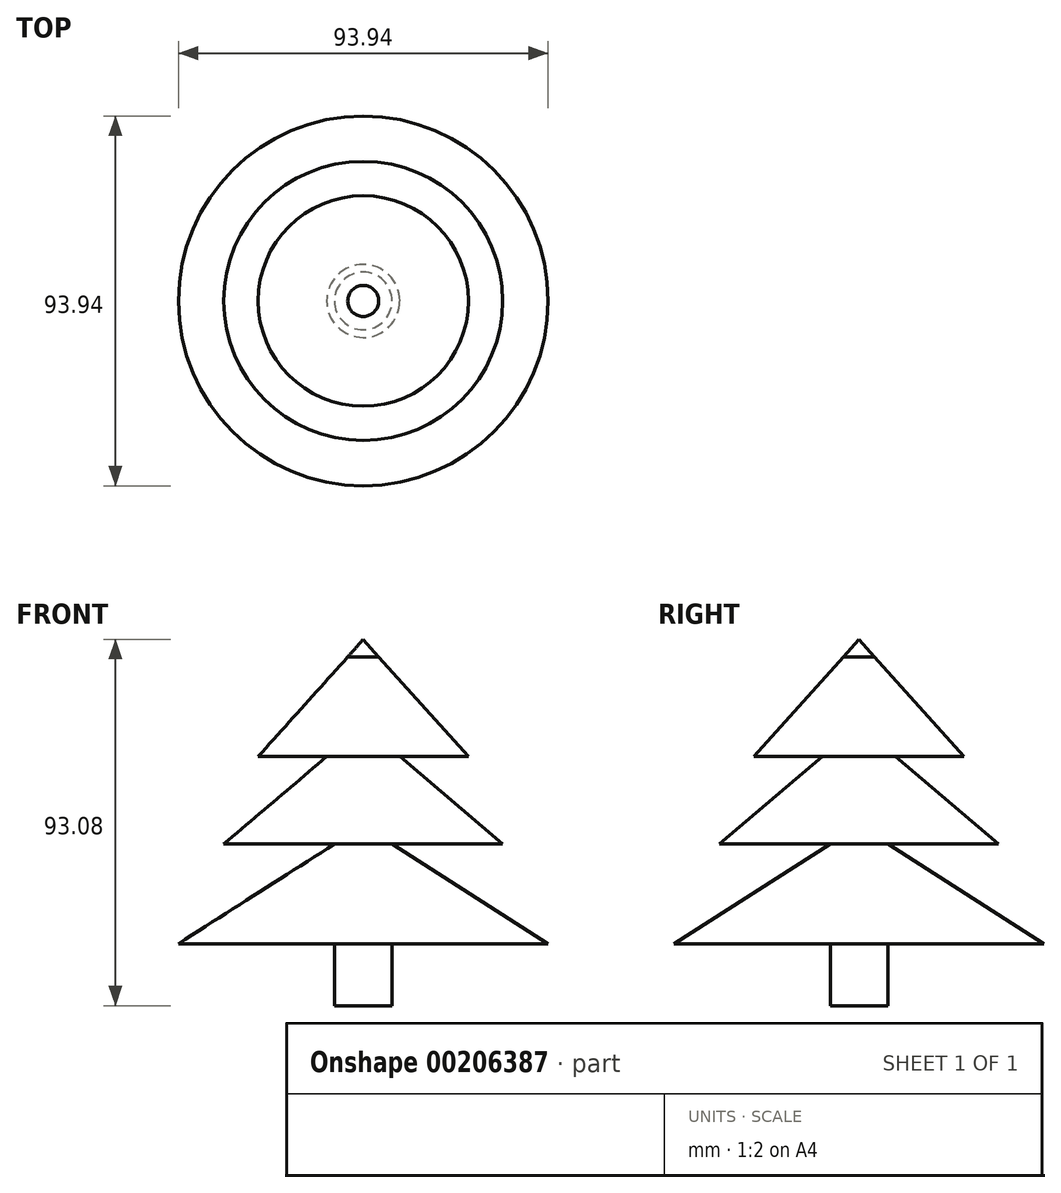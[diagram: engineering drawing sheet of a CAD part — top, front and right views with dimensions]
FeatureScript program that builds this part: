
annotation { "Feature Type Name" : "Feature", "Feature Type Description" : "" }
export const myFeature = defineFeature(function(context is Context, id is Id, definition is map)
    precondition{}
    {
        {
            var Q0;
            Q0=qCreatedBy(makeId("Front.planeOp"),FACE);
            var sketch = newSketch(context, id + "F0", { "sketchPlane" : qUnion([Q0])});
            skLineSegment(sketch, "E0", {"start": v(-3.94, 53.57) * mm, "end": v(-26.72, 28.26) * mm});
            skLineSegment(sketch, "E1", {"start": v(-26.72, 28.26) * mm, "end": v(-9.28, 28.26) * mm});
            skLineSegment(sketch, "E2", {"start": v(-9.28, 28.26) * mm, "end": v(-35.44, 6.05) * mm});
            skLineSegment(sketch, "E3", {"start": v(-35.44, 6.05) * mm, "end": v(-7.31, 6.05) * mm});
            skLineSegment(sketch, "E4", {"start": v(-7.31, 6.05) * mm, "end": v(-46.97, -19.26) * mm});
            skLineSegment(sketch, "E5", {"start": v(-46.97, -19.26) * mm, "end": v(0, -19.26) * mm});
            skLineSegment(sketch, "E6", {"start": v(-3.94, 53.57) * mm, "end": v(0, 58.07) * mm});
            skLineSegment(sketch, "E7", {"start": v(-7.31, -19.26) * mm, "end": v(-7.31, -35.01) * mm});
            skLineSegment(sketch, "E8", {"start": v(-7.31, -35.01) * mm, "end": v(0, -35.01) * mm});
            skLineSegment(sketch, "E9", {"start": v(0, -35.01) * mm, "end": v(0, -19.26) * mm});
            skLineSegment(sketch, "E10", {"start": v(0, -19.26) * mm, "end": v(0, 58.07) * mm});
            skSolve(sketch);
        }
        {
            var Q0;
            Q0=makeQuery(id+"F0.imprint","IMPRINT",FACE,{"disambiguationData":[TD([[makeQuery(id+"F0.imprint","IMPRINT",EDGE,{"derivedFrom":sQuery(id+"F0.wireOp",EDGE,"E0")}),1.0]])]});
            var Q1;
            {var subQ2=sQuery(id+"F0.wireOp",EDGE,"E7");Q1=makeQuery(id+"F0.imprint","IMPRINT",FACE,{"disambiguationData":[TD([[makeQuery(id+"F0.imprint","IMPRINT",EDGE,{"derivedFrom":subQ2}),1.0]])]});}
            var Q2;
            Q2=sQuery(id+"F0.wireOp",EDGE,"E10");
            revolve(context, id + "F1", {"entities" : qUnion([Q0, Q1]), "axis" : qUnion([Q2]), "revolveType" : RevolveType.FULL});
        }
    });
